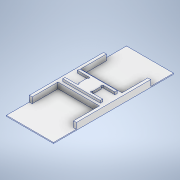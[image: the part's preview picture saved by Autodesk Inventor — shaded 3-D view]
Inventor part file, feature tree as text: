
AUTODESK INVENTOR PART (.ipt)
format: ipt  version: 2020.1 (Build 241239000, 239)  size: 186,880 bytes
history: native  units: mm
features: extrude x4, sketch x4, projected_geometry x2, other x1
ambient origin geometry x8: Origin, YZ Plane, XZ Plane, XY Plane, X Axis, Y Axis, Z Axis, Center Point
bodies: Body1 (feature_tree)
feature tree (11):
  other  "Твердое тело1"
  extrude  "Выдавливание1"  Depth=516.0mm
  extrude  "Выдавливание2"  Depth=29.0mm
  extrude  "Выдавливание3"  Depth=200.0mm TaperAngle=0.0deg
  extrude  "Выдавливание4"  Depth=52.0mm
  sketch  "Эскиз1"
  sketch  "Эскиз2"
  projected_geometry  "Спроецированная петля1"
  sketch  "Эскиз3"
  projected_geometry  "Спроецированная петля2"
  sketch  "Эскиз4"
